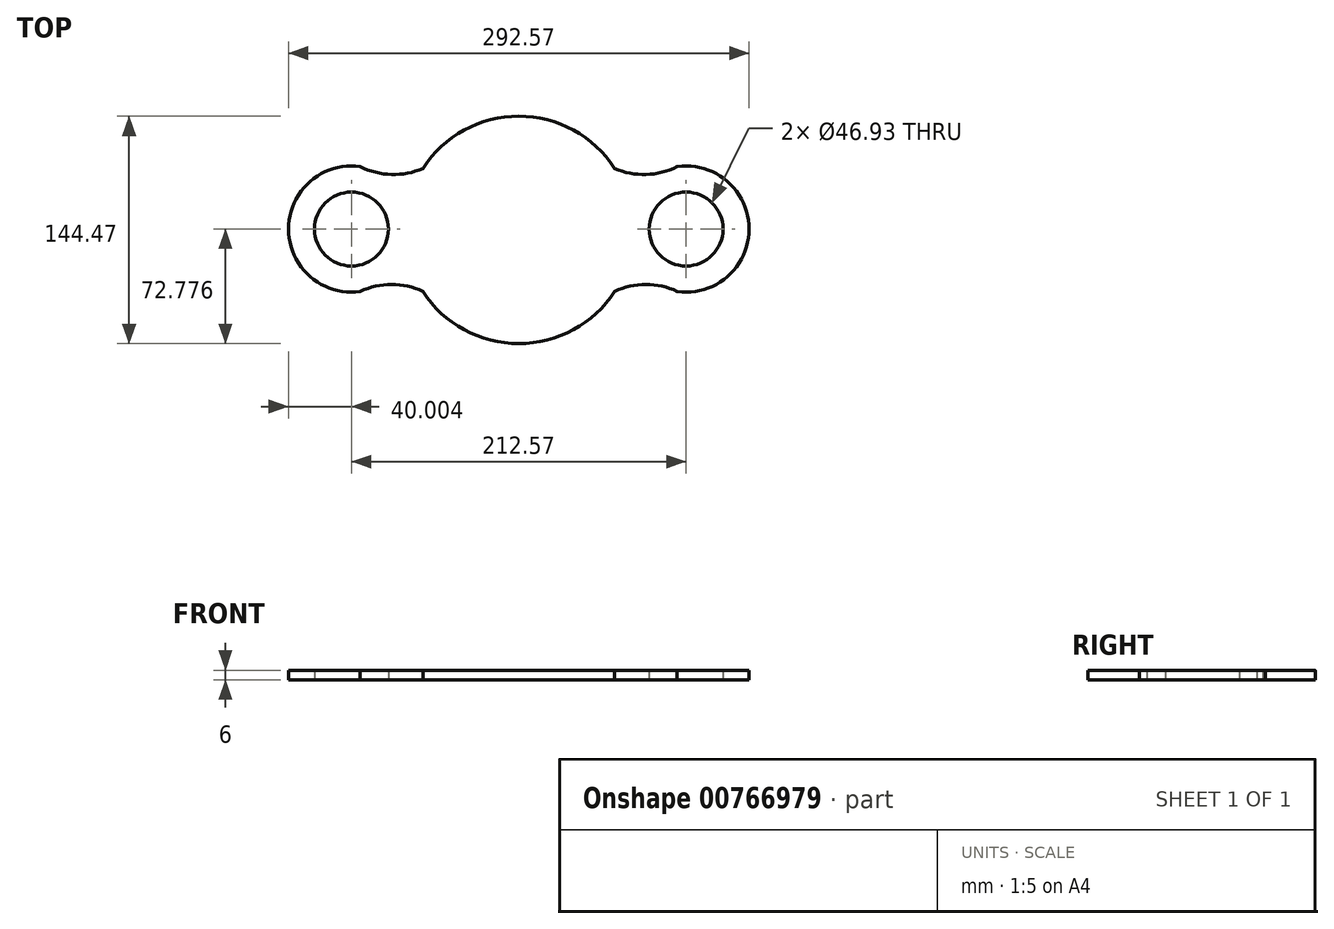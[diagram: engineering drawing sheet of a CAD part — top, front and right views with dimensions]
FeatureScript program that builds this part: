
annotation { "Feature Type Name" : "Feature", "Feature Type Description" : "" }
export const myFeature = defineFeature(function(context is Context, id is Id, definition is map)
    precondition{}
    {
        {
            var Q0;
            Q0=qCreatedBy(makeId("Top.planeOp"),FACE);
            var sketch = newSketch(context, id + "F0", { "sketchPlane" : qUnion([Q0])});
            skArc(sketch, "E0", {"start": v(-47.15, -34.26) * mm, "mid": v(-20.95, -58.62) * mm, "end": v(13.73, -67.43) * mm});
            skArc(sketch, "E1.trimOffspring", {"start": v(13.73, 77.03) * mm, "mid": v(-20.95, 68.23) * mm, "end": v(-47.15, 43.86) * mm});
            skPoint(sketch, "E2", {"position": v(-47.15, 43.86) * mm});
            skPoint(sketch, "E3", {"position": v(-47.15, -34.26) * mm});
            skArc(sketch, "E4", {"start": v(-86.93, 44.95) * mm, "mid": v(-67.16, 39.99) * mm, "end": v(-47.15, 43.86) * mm});
            skArc(sketch, "E5", {"start": v(-47.15, -34.26) * mm, "mid": v(-67.04, -29.84) * mm, "end": v(-86.93, -34.26) * mm});
            skArc(sketch, "E6", {"start": v(-86.93, 44.95) * mm, "mid": v(-132.56, 5.35) * mm, "end": v(-86.93, -34.26) * mm});
            skArc(sketch, "E7", {"start": v(13.73, 36.06) * mm, "mid": v(-17.65, 4.8) * mm, "end": v(13.73, -26.45) * mm});
            skCircle(sketch, "E8", {"center": v(-92.56, 5.35) * mm, "radius": 23.46 * mm});
            skPoint(sketch, "E9.MirrorP", {"position": v(74.6, -34.26) * mm});
            skArc(sketch, "E10.MirrorCS", {"start": v(74.6, -34.26) * mm, "mid": v(94.5, -29.84) * mm, "end": v(114.38, -34.26) * mm});
            skArc(sketch, "E11.MirrorCS", {"start": v(13.73, 36.06) * mm, "mid": v(45.1, 4.8) * mm, "end": v(13.73, -26.45) * mm});
            skCircle(sketch, "E12.MirrorC", {"center": v(120.01, 5.35) * mm, "radius": 23.46 * mm});
            skPoint(sketch, "E13.MirrorP", {"position": v(74.6, 43.86) * mm});
            skArc(sketch, "E14.MirrorCS", {"start": v(13.73, 77.03) * mm, "mid": v(48.4, 68.23) * mm, "end": v(74.6, 43.86) * mm});
            skArc(sketch, "E15.MirrorCS", {"start": v(114.38, 44.95) * mm, "mid": v(94.62, 39.99) * mm, "end": v(74.6, 43.86) * mm});
            skArc(sketch, "E16.MirrorCS", {"start": v(114.38, 44.95) * mm, "mid": v(160.01, 5.35) * mm, "end": v(114.38, -34.26) * mm});
            skArc(sketch, "E17.MirrorCS", {"start": v(74.6, -34.26) * mm, "mid": v(48.4, -58.62) * mm, "end": v(13.73, -67.43) * mm});
            skSolve(sketch);
        }
        {
            var Q0;
            Q0=makeQuery(id+"F0.imprint","IMPRINT",FACE,{"disambiguationData":[TD([[makeQuery(id+"F0.imprint","IMPRINT",EDGE,{"derivedFrom":sQuery(id+"F0.wireOp",EDGE,"E0")}),1.0]])]});
            extrude(context, id + "F1", {"entities" : qUnion([Q0]), "depth" : 6 * mm, "offsetDistance" : 25 * mm});
        }
    });
